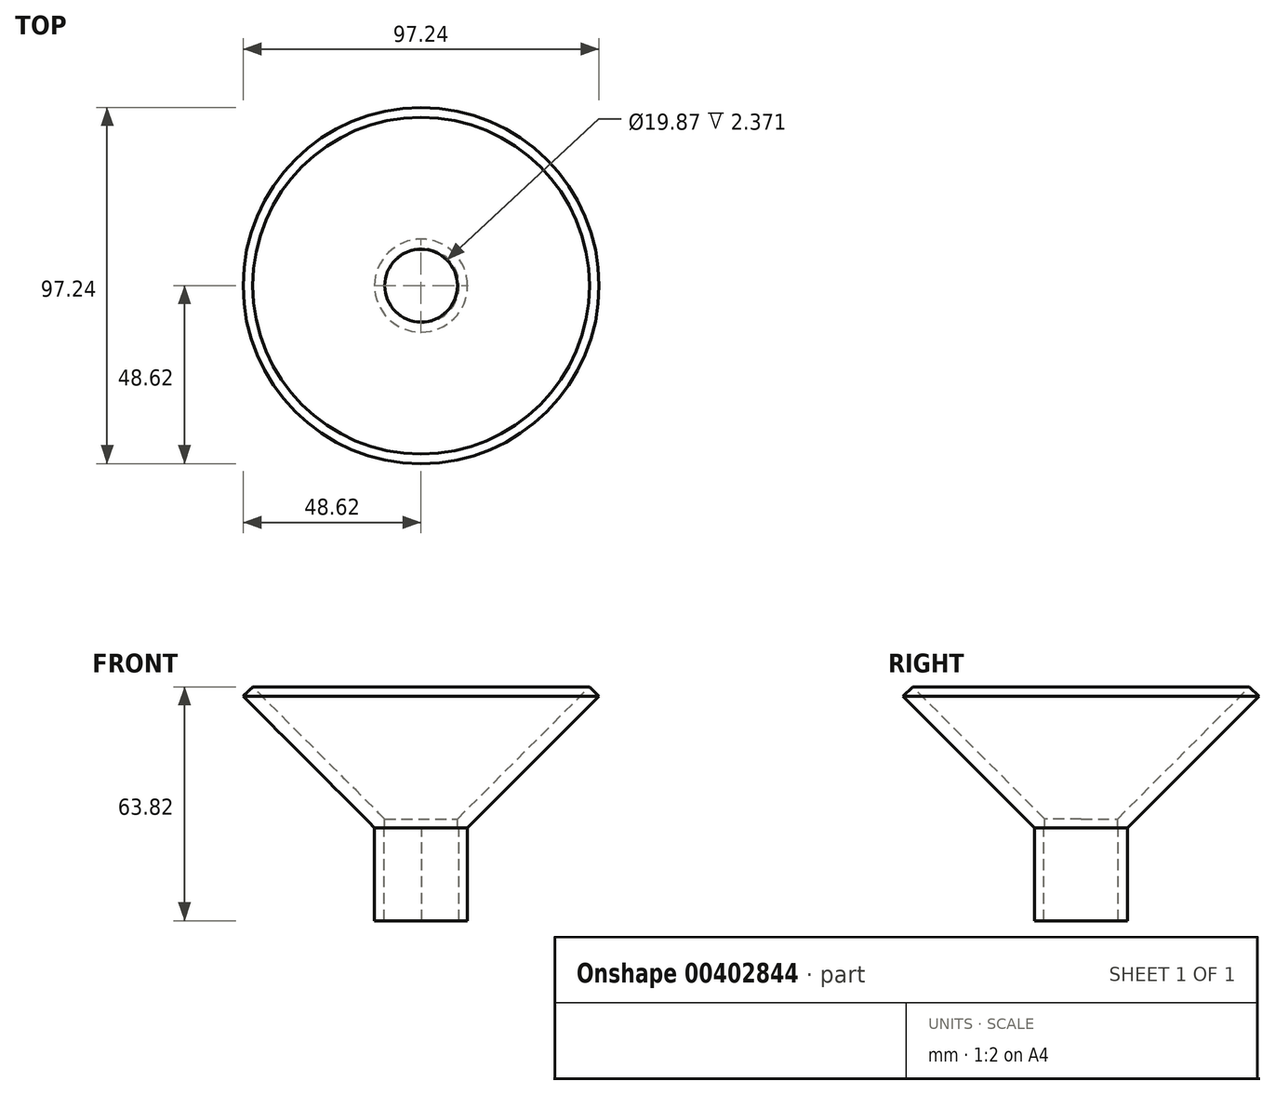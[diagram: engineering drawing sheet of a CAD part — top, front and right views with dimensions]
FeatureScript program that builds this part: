
annotation { "Feature Type Name" : "Feature", "Feature Type Description" : "" }
export const myFeature = defineFeature(function(context is Context, id is Id, definition is map)
    precondition{}
    {
        {
            var Q0;
            Q0=qCreatedBy(makeId("Front.planeOp"),FACE);
            var sketch = newSketch(context, id + "F0", { "sketchPlane" : qUnion([Q0])});
            skLineSegment(sketch, "E0", {"start": v(35.92, 35.92) * mm, "end": v(0, 0) * mm});
            skLineSegment(sketch, "E1", {"start": v(0, 0) * mm, "end": v(0, -25.4) * mm});
            skLineSegment(sketch, "E2", {"start": v(0, -25.4) * mm, "end": v(-12.7, -25.4) * mm});
            skLineSegment(sketch, "E3", {"start": v(-12.7, -25.4) * mm, "end": v(-12.7, 2.37) * mm});
            skLineSegment(sketch, "E4", {"start": v(-12.7, 2.37) * mm, "end": v(-2.77, 2.37) * mm});
            skLineSegment(sketch, "E5", {"start": v(-2.77, 2.37) * mm, "end": v(33.29, 38.42) * mm});
            skLineSegment(sketch, "E6", {"start": v(33.29, 38.42) * mm, "end": v(35.92, 35.92) * mm});
            skSolve(sketch);
        }
        {
            var Q0;
            Q0=makeQuery(id+"F0.imprint","IMPRINT",FACE,{"disambiguationData":[TD([[makeQuery(id+"F0.imprint","IMPRINT",EDGE,{"derivedFrom":sQuery(id+"F0.wireOp",EDGE,"E0")}),-1.0]])]});
            var Q1;
            Q1=sQuery(id+"F0.wireOp",EDGE,"E3");
            revolve(context, id + "F1", {"entities" : qUnion([Q0]), "axis" : qUnion([Q1]), "revolveType" : RevolveType.FULL});
        }
        {
            var Q0;
            Q0=qCreatedBy(makeId("Top.planeOp"),FACE);
            var sketch = newSketch(context, id + "F2", { "sketchPlane" : qUnion([Q0])});
            skCircle(sketch, "E7", {"center": v(-12.64, 0) * mm, "radius": 10.16 * mm});
            skSolve(sketch);
        }
        {
            var Q0;
            Q0 = qSketchRegion(id + "F2", true);
            extrude(context, id + "F3", {"entities" : qUnion([Q0]), "operationType" : NewBodyOperationType.REMOVE, "oppositeDirection" : true, "depth" : 50.8 * mm});
        }
        {
            var Q0;
            Q0=qCreatedBy(makeId("Top.planeOp"),FACE);
            var sketch = newSketch(context, id + "F4", { "sketchPlane" : qUnion([Q0])});
            skCircle(sketch, "E8", {"center": v(-12.45, 0) * mm, "radius": 10.16 * mm});
            skSolve(sketch);
        }
        {
            var Q0;
            Q0 = qSketchRegion(id + "F4", true);
            extrude(context, id + "F5", {"entities" : qUnion([Q0]), "operationType" : NewBodyOperationType.REMOVE, "oppositeDirection" : true, "depth" : 25.4 * mm});
        }
        {
            var Q0;
            Q0=makeQuery(id+"F1.opRevolve","SWEPT_FACE",FACE,{"disambiguationData":[OSD([sQuery(id+"F0.wireOp",EDGE,"E4")])]});
            extrude(context, id + "F6", {"entities" : qUnion([Q0]), "operationType" : NewBodyOperationType.REMOVE, "oppositeDirection" : true, "depth" : 25.4 * mm});
        }
    });
